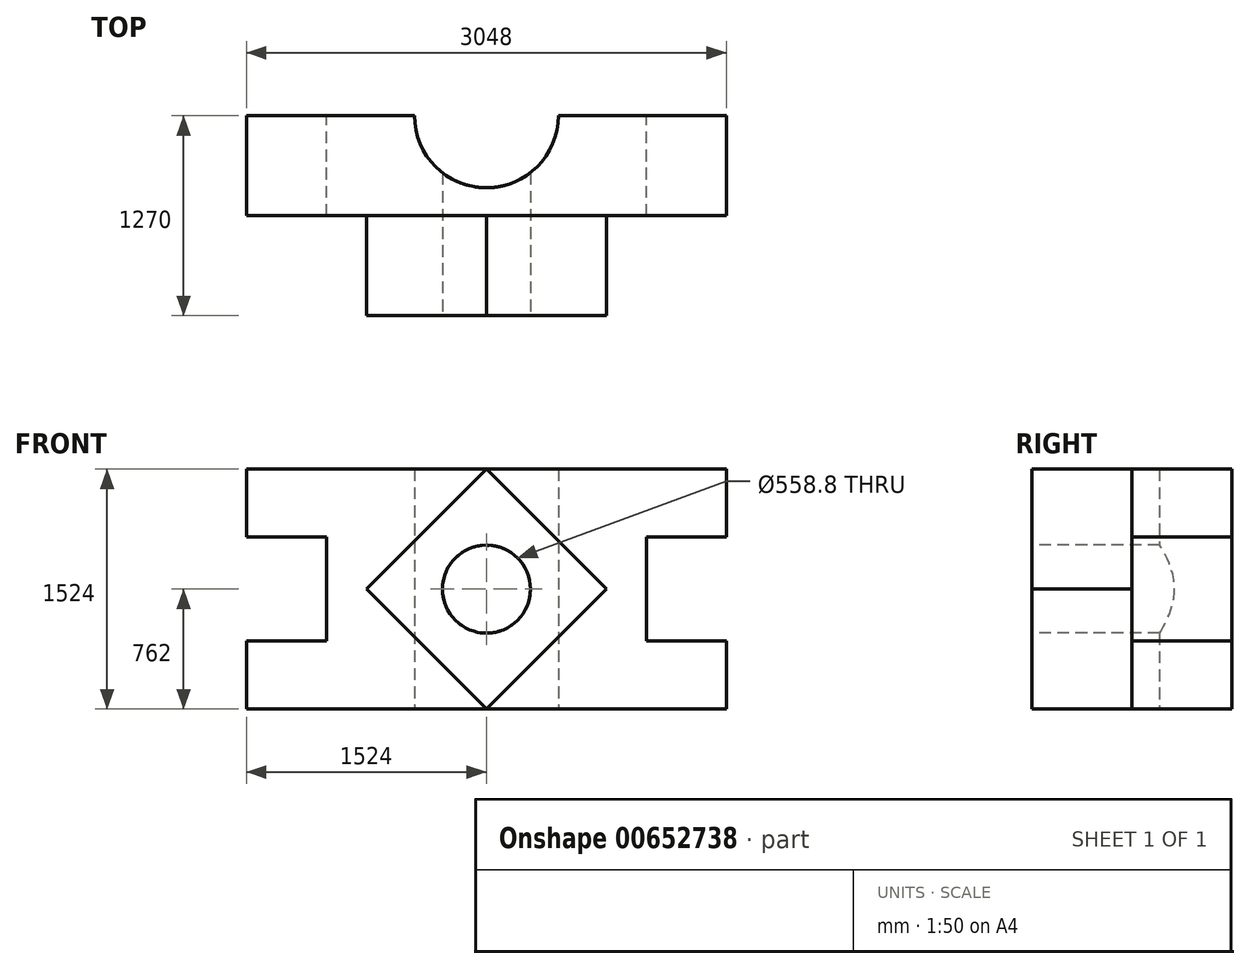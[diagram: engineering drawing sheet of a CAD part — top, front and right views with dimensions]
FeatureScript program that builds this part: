
annotation { "Feature Type Name" : "Feature", "Feature Type Description" : "" }
export const myFeature = defineFeature(function(context is Context, id is Id, definition is map)
    precondition{}
    {
        {
            var Q0;
            Q0=qCreatedBy(makeId("Front.planeOp"),FACE);
            var sketch = newSketch(context, id + "F0", { "sketchPlane" : qUnion([Q0])});
            skLineSegment(sketch, "E0.bottom", {"start": v(1524, -762) * mm, "end": v(-1524, -762) * mm});
            skLineSegment(sketch, "E0.top", {"start": v(1524, 762) * mm, "end": v(-1524, 762) * mm});
            skLineSegment(sketch, "E0.left", {"start": v(1524, -762) * mm, "end": v(1524, -330.2) * mm});
            skLineSegment(sketch, "E0.right", {"start": v(-1524, -762) * mm, "end": v(-1524, -330.2) * mm});
            skPoint(sketch, "E0.middle", {"position": v(0, 0) * mm});
            skLineSegment(sketch, "E1.bottom", {"start": v(-1016, -330.2) * mm, "end": v(-1524, -330.2) * mm});
            skLineSegment(sketch, "E1.top", {"start": v(-1016, 330.2) * mm, "end": v(-1524, 330.2) * mm});
            skLineSegment(sketch, "E1.left", {"start": v(-1016, -330.2) * mm, "end": v(-1016, 330.2) * mm});
            skPoint(sketch, "E1.middle", {"position": v(-1524, 0) * mm});
            skPoint(sketch, "E1.right.end.orphan", {"position": v(-2032, 330.2) * mm});
            skPoint(sketch, "E2.orphan", {"position": v(-2032, -330.2) * mm});
            skLineSegment(sketch, "E3.trimOffspring", {"start": v(-1524, 330.2) * mm, "end": v(-1524, 762) * mm});
            skLineSegment(sketch, "E4.bottom", {"start": v(1524, -330.2) * mm, "end": v(1016, -330.2) * mm});
            skLineSegment(sketch, "E4.top", {"start": v(1524, 330.2) * mm, "end": v(1016, 330.2) * mm});
            skLineSegment(sketch, "E4.right", {"start": v(1016, -330.2) * mm, "end": v(1016, 330.2) * mm});
            skPoint(sketch, "E4.middle", {"position": v(1524, 0) * mm});
            skLineSegment(sketch, "E5.trimOffspring", {"start": v(1524, 330.2) * mm, "end": v(1524, 762) * mm});
            skPoint(sketch, "E6.orphan", {"position": v(2032, -330.2) * mm});
            skPoint(sketch, "E7.orphan", {"position": v(2032, 330.2) * mm});
            skSolve(sketch);
        }
        {
            var Q0;
            Q0=makeQuery(id+"F0.imprint","IMPRINT",FACE,{"disambiguationData":[TD([[makeQuery(id+"F0.imprint","IMPRINT",EDGE,{"derivedFrom":sQuery(id+"F0.wireOp",EDGE,"E0.bottom")}),-1.0]])]});
            extrude(context, id + "F1", {"entities" : qUnion([Q0]), "depth" : 635 * mm, "offsetDistance" : 25.4 * mm});
        }
        {
            var Q0;
            Q0=makeQuery(id+"F1.opExtrude","SWEPT_FACE",FACE,{"disambiguationData":[OSD([sQuery(id+"F0.wireOp",EDGE,"E0.bottom")])]});
            var sketch = newSketch(context, id + "F2", { "sketchPlane" : qUnion([Q0])});
            skArc(sketch, "E8", {"start": v(457.2, 0) * mm, "mid": v(0, 457.2) * mm, "end": v(-457.2, 0) * mm});
            skSolve(sketch);
        }
        {
            var Q0;
            {var subQ0=sQuery(id+"F2.wireOp",EDGE,"E8");Q0=makeQuery(id+"F2.imprint","IMPRINT",FACE,{"disambiguationData":[TD([[makeQuery(id+"F2.imprint","IMPRINT",EDGE,{"derivedFrom":subQ0}),1.0]])]});}
            extrude(context, id + "F3", {"entities" : qUnion([Q0]), "operationType" : NewBodyOperationType.REMOVE, "endBound" : BoundingType.THROUGH_ALL, "oppositeDirection" : true, "depth" : 25.4 * mm, "offsetDistance" : 25.4 * mm});
        }
        {
            var Q0;
            Q0=makeQuery(id+"F1.opExtrude","CAP_FACE",FACE,{"disambiguationData":[OSD([sQuery(id+"F0.wireOp",EDGE,"E0.bottom"),sQuery(id+"F0.wireOp",EDGE,"E0.top"),sQuery(id+"F0.wireOp",EDGE,"E0.left"),sQuery(id+"F0.wireOp",EDGE,"E0.right"),sQuery(id+"F0.wireOp",EDGE,"E1.bottom"),sQuery(id+"F0.wireOp",EDGE,"E1.top"),sQuery(id+"F0.wireOp",EDGE,"E1.left"),sQuery(id+"F0.wireOp",EDGE,"E3.trimOffspring"),sQuery(id+"F0.wireOp",EDGE,"E4.bottom"),sQuery(id+"F0.wireOp",EDGE,"E4.top"),sQuery(id+"F0.wireOp",EDGE,"E4.right"),sQuery(id+"F0.wireOp",EDGE,"E5.trimOffspring")])],"isStart":false});
            var sketch = newSketch(context, id + "F4", { "sketchPlane" : qUnion([Q0])});
            skLineSegment(sketch, "E9", {"start": v(0, 762) * mm, "end": v(-762, 0) * mm});
            skLineSegment(sketch, "E10", {"start": v(-762, 0) * mm, "end": v(0, -762) * mm});
            skLineSegment(sketch, "E11", {"start": v(0, -762) * mm, "end": v(762, 0) * mm});
            skLineSegment(sketch, "E12", {"start": v(762, 0) * mm, "end": v(0, 762) * mm});
            skPoint(sketch, "E13.end.orphan", {"position": v(762, -762) * mm});
            skPoint(sketch, "E14.end.orphan", {"position": v(-762, -762) * mm});
            skPoint(sketch, "E15.end.orphan", {"position": v(762, 762) * mm});
            skPoint(sketch, "E16.end.orphan", {"position": v(-762, 762) * mm});
            skSolve(sketch);
        }
        {
            var Q0;
            Q0=makeQuery(id+"F4.imprint","IMPRINT",FACE,{"disambiguationData":[TD([[makeQuery(id+"F4.imprint","IMPRINT",EDGE,{"derivedFrom":sQuery(id+"F4.wireOp",EDGE,"E9")}),1.0]])]});
            extrude(context, id + "F5", {"entities" : qUnion([Q0]), "operationType" : NewBodyOperationType.ADD, "depth" : 635 * mm, "offsetDistance" : 25.4 * mm});
        }
        {
            var Q0;
            Q0=makeQuery(id+"F5.opExtrude","CAP_FACE",FACE,{"disambiguationData":[OSD([sQuery(id+"F4.wireOp",EDGE,"E9"),sQuery(id+"F4.wireOp",EDGE,"E10"),sQuery(id+"F4.wireOp",EDGE,"E11"),sQuery(id+"F4.wireOp",EDGE,"E12")])],"isStart":false});
            var sketch = newSketch(context, id + "F6", { "sketchPlane" : qUnion([Q0])});
            skCircle(sketch, "E17", {"center": v(0, 0) * mm, "radius": 279.4 * mm});
            skSolve(sketch);
        }
        {
            var Q0;
            Q0=makeQuery(id+"F6.imprint","IMPRINT",FACE,{"disambiguationData":[TD([[makeQuery(id+"F6.imprint","IMPRINT",EDGE,{"derivedFrom":sQuery(id+"F6.wireOp",EDGE,"E17")}),1.0]])]});
            extrude(context, id + "F7", {"entities" : qUnion([Q0]), "operationType" : NewBodyOperationType.REMOVE, "endBound" : BoundingType.THROUGH_ALL, "oppositeDirection" : true, "depth" : 25.4 * mm, "offsetDistance" : 25.4 * mm});
        }
    });
